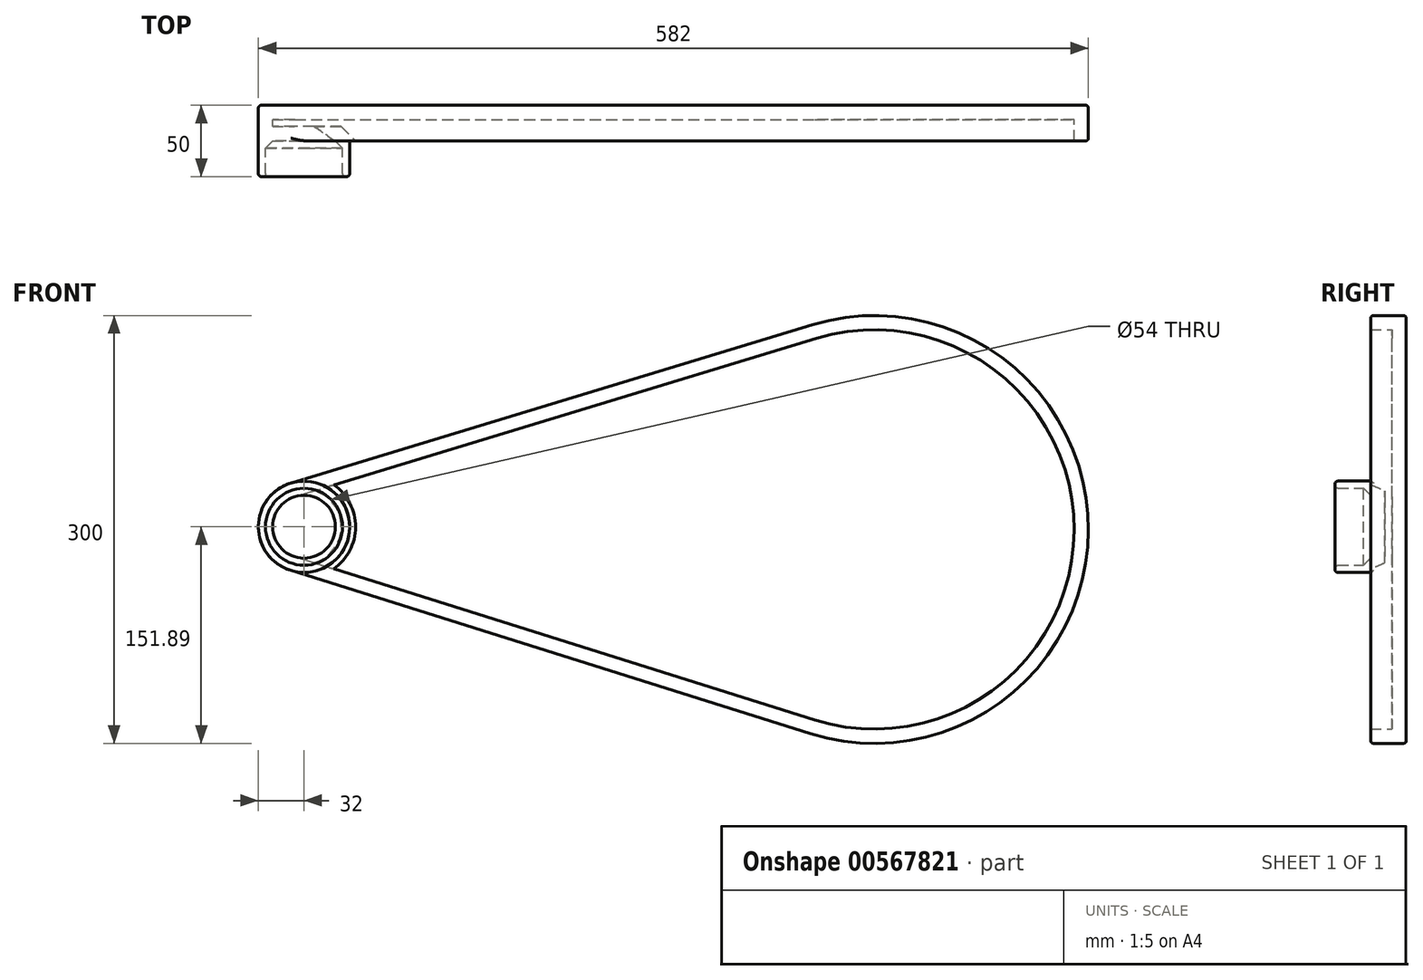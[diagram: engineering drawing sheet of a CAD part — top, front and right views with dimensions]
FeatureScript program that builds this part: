
annotation { "Feature Type Name" : "Feature", "Feature Type Description" : "" }
export const myFeature = defineFeature(function(context is Context, id is Id, definition is map)
    precondition{}
    {
        {
            var Q0;
            Q0=qCreatedBy(makeId("Front.planeOp"),FACE);
            var sketch = newSketch(context, id + "F0", { "sketchPlane" : qUnion([Q0])});
            skLineSegment(sketch, "E0", {"start": v(0, 0) * mm, "end": v(400, -1.9) * mm, "construction": true});
            skCircle(sketch, "E1", {"center": v(400, -1.9) * mm, "radius": 150 * mm});
            skCircle(sketch, "E2", {"center": v(0, 0) * mm, "radius": 32 * mm});
            skLineSegment(sketch, "E3", {"start": v(356.42, 141.64) * mm, "end": v(-9.3, 30.62) * mm});
            skLineSegment(sketch, "E4", {"start": v(-9.58, -30.53) * mm, "end": v(355.07, -145) * mm});
            skSolve(sketch);
        }
        {
            var Q0;
            Q0 = qSketchRegion(id + "F0", true);
            extrude(context, id + "F1", {"entities" : qUnion([Q0]), "depth" : 25 * mm, "offsetDistance" : 25 * mm});
        }
        {
            var Q0;
            Q0=makeQuery(id+"F1.opExtrude","CAP_FACE",FACE,{"disambiguationData":[OSD([sQuery(id+"F0.wireOp",EDGE,"E1"),sQuery(id+"F0.wireOp",EDGE,"E2"),sQuery(id+"F0.wireOp",EDGE,"E3"),sQuery(id+"F0.wireOp",EDGE,"E4")])],"isStart":false});
            var sketch = newSketch(context, id + "F2", { "sketchPlane" : qUnion([Q0])});
            skCircle(sketch, "E5.0", {"center": v(0, 0) * mm, "radius": 32 * mm});
            skCircle(sketch, "E6.0", {"center": v(0, 0) * mm, "radius": 27 * mm});
            skSolve(sketch);
        }
        {
            var Q0;
            Q0=makeQuery(id+"F2.imprint","IMPRINT",FACE,{"disambiguationData":[TD([[makeQuery(id+"F2.imprint","IMPRINT",EDGE,{"derivedFrom":sQuery(id+"F2.wireOp",EDGE,"E6.0")}),-1.0]])]});
            extrude(context, id + "F3", {"entities" : qUnion([Q0]), "operationType" : NewBodyOperationType.ADD, "depth" : 25 * mm, "offsetDistance" : 25 * mm});
        }
        {
            var Q0;
            Q0=makeQuery(id+"F3.opExtrude","CAP_EDGE",EDGE,{"disambiguationData":[OSD([sQuery(id+"F2.wireOp",EDGE,"E5.0")])],"isStart":false});
            var Q1;
            Q1=makeQuery(id+"F3.opExtrude","CAP_EDGE",EDGE,{"disambiguationData":[OSD([sQuery(id+"F2.wireOp",EDGE,"E6.0")])],"isStart":false});
            var Q2;
            Q2=makeQuery(id+"F3.opExtrude","CAP_EDGE",EDGE,{"disambiguationData":[OSD([sQuery(id+"F2.wireOp",EDGE,"E5.0")])],"isStart":true});
            var Q3;
            Q3=makeQuery(id+"F1.opExtrude","CAP_EDGE",EDGE,{"disambiguationData":[OSD([sQuery(id+"F0.wireOp",EDGE,"E4")])],"isStart":false});
            var Q4;
            Q4=makeQuery(id+"F1.opExtrude","CAP_EDGE",EDGE,{"disambiguationData":[OSD([sQuery(id+"F0.wireOp",EDGE,"E4")])],"isStart":true});
            fillet(context, id + "F4", {"entities" : qUnion([Q0, Q1, Q2, Q3, Q4]), "radius" : 2 * mm, "tangentPropagation" : true, "allowEdgeOverflow" : false});
        }
        {
            var Q0;
            Q0=makeQuery(id+"F3.opExtrude","CAP_EDGE",EDGE,{"disambiguationData":[OSD([sQuery(id+"F2.wireOp",EDGE,"E6.0")])],"isStart":true});
            chamfer(context, id + "F5", {"entities" : qUnion([Q0]), "width" : 5 * mm, "tangentPropagation" : true});
        }
        {
            var Q0;
            {var subQ0=sQuery(id+"F0.wireOp",EDGE,"E3");var subQ1=sQuery(id+"F0.wireOp",EDGE,"E2");var subQ2=sQuery(id+"F0.wireOp",EDGE,"E4");var subQ3=sQuery(id+"F0.wireOp",EDGE,"E1");Q0=makeQuery(id+"F3.boolean.opBoolean","SPLIT",FACE,{"disambiguationData":[TD([makeQuery(id+"F1.opExtrude","SWEPT_FACE",FACE,{"disambiguationData":[OSD([subQ3])]})])],"derivedFrom":makeQuery(id+"F1.opExtrude","CAP_FACE",FACE,{"disambiguationData":[OSD([subQ3,subQ1,subQ0,subQ2])],"isStart":false})});}
            shell(context, id + "F6", {"entities" : qUnion([Q0]), "thickness" : 10 * mm});
        }
    });
